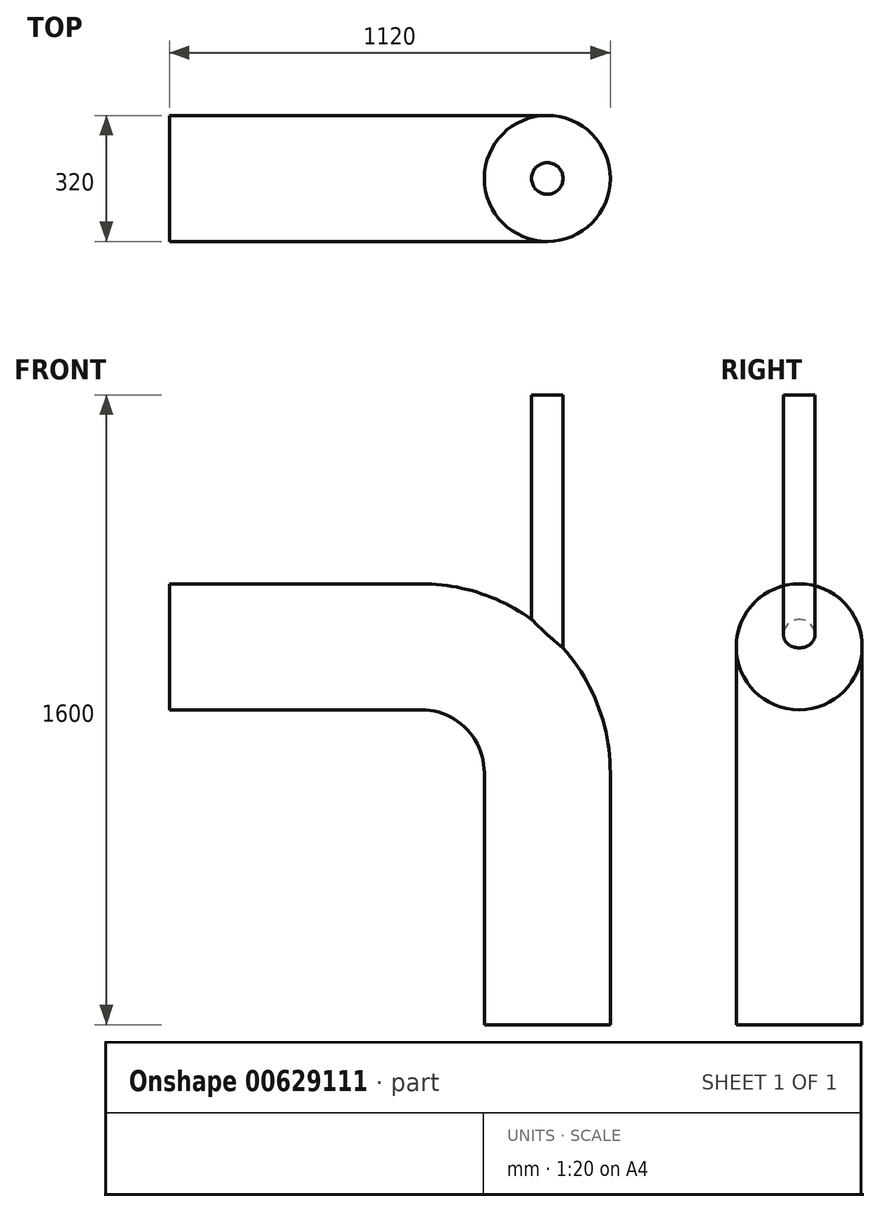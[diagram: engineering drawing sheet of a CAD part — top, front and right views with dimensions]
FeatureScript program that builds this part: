
annotation { "Feature Type Name" : "Feature", "Feature Type Description" : "" }
export const myFeature = defineFeature(function(context is Context, id is Id, definition is map)
    precondition{}
    {
        {
            var Q0;
            Q0=qCreatedBy(makeId("Front.planeOp"),FACE);
            var sketch = newSketch(context, id + "F0", { "sketchPlane" : qUnion([Q0])});
            skLineSegment(sketch, "E0", {"start": v(-640, 0) * mm, "end": v(0, 0) * mm});
            skLineSegment(sketch, "E1", {"start": v(320, -320) * mm, "end": v(320, -960) * mm});
            skArc(sketch, "E2", {"start": v(0, 0) * mm, "mid": v(226.27, -93.73) * mm, "end": v(320, -320) * mm});
            skSolve(sketch);
        }
        {
            var Q0;
            Q0=qCreatedBy(makeId("Right.planeOp"),FACE);
            var sketch = newSketch(context, id + "F1", { "sketchPlane" : qUnion([Q0])});
            skCircle(sketch, "E3", {"center": v(0, 0) * mm, "radius": 160 * mm});
            skSolve(sketch);
        }
        {
            var Q0;
            Q0=makeQuery(id+"F1.imprint","IMPRINT",FACE,{"disambiguationData":[TD([[makeQuery(id+"F1.imprint","IMPRINT",EDGE,{"derivedFrom":sQuery(id+"F1.wireOp",EDGE,"E3")}),1.0]])]});
            var Q1;
            Q1 = qConstructionFilter(qBodyType(qCreatedBy(id + "F0" ,EDGE), BodyType.WIRE), ConstructionObject.NO);
            sweep(context, id + "F2", {"profiles" : qUnion([Q0]), "path" : qUnion([Q1])});
        }
        {
            var Q0;
            Q0=qCreatedBy(makeId("Front.planeOp"),FACE);
            var sketch = newSketch(context, id + "F3", { "sketchPlane" : qUnion([Q0])});
            skLineSegment(sketch, "E4", {"start": v(320, 640) * mm, "end": v(320, -183.25) * mm});
            skSolve(sketch);
        }
        {
            var Q0;
            Q0=qCreatedBy(makeId("Top.planeOp"),FACE);
            var sketch = newSketch(context, id + "F4", { "sketchPlane" : qUnion([Q0])});
            skCircle(sketch, "E5", {"center": v(320, 0) * mm, "radius": 40 * mm});
            skSolve(sketch);
        }
        {
            var Q0;
            Q0=makeQuery(id+"F4.imprint","IMPRINT",FACE,{"disambiguationData":[TD([[makeQuery(id+"F4.imprint","IMPRINT",EDGE,{"derivedFrom":sQuery(id+"F4.wireOp",EDGE,"E5")}),1.0]])]});
            var Q1;
            Q1 = qConstructionFilter(qBodyType(qCreatedBy(id + "F3" ,EDGE), BodyType.WIRE), ConstructionObject.NO);
            sweep(context, id + "F5", {"operationType" : NewBodyOperationType.ADD, "profiles" : qUnion([Q0]), "path" : qUnion([Q1])});
        }
    });
